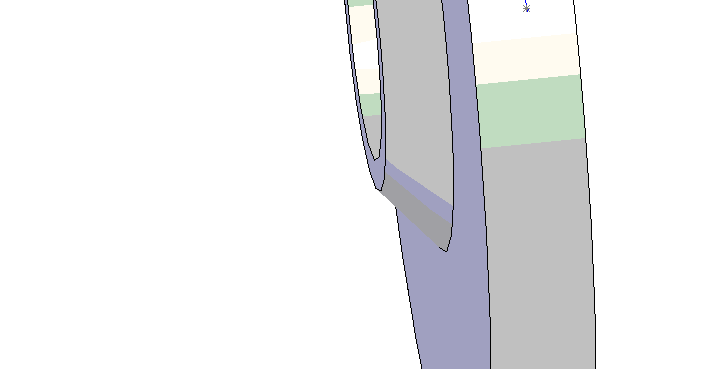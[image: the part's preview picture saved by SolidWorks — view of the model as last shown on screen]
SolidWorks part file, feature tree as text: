
SOLIDWORKS PART (.sldprt)
format: sldprt  version: not decoded by parser v0  size: 210,432 bytes
history: native  units: mm
features: sketch x4, cut_extrude x2, extrude x1, revolve x1 (+11 scaffold rows collapsed)
feature tree (19):
  scaffold x11  (default folders/planes/origin — collapsed)
  sketch  "Sketch1"  dims[D1=23.75mm]
  extrude  "Extrude1"  Depth=5mm
  sketch  "Sketch2"  dims[D1=6.35mm]
  cut_extrude  "Cut-Extrude1"  Depth=13mm
  sketch  "Sketch4"  dims[D1=9.525mm]
  cut_extrude  "Cut-Extrude3"  Depth=5mm
  sketch  "Sketch5"  dims[D1=~2.80543mm]
  revolve  "Revolve1"  Angle=360deg
decode coverage: 8 of 8 modeling features carry decoded parameters
note: ~ marks probable driven/reference dimensions
note: suppression state not decoded; provenance and decode notes live in map.json
